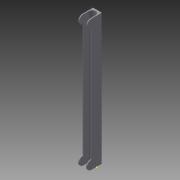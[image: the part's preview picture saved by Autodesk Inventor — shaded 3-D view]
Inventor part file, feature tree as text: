
AUTODESK INVENTOR PART (.ipt)
format: ipt  version: 2015 (Build 190159000, 159)  size: 121,856 bytes
history: native  units: mm
features: sketch x6, extrude x5, fillet x2
ambient origin geometry x8: Origin, YZ Plane, XZ Plane, XY Plane, X Axis, Y Axis, Z Axis, Center Point
bodies: Body1 (feature_tree)
feature tree (13):
  extrude  "Extrusion3"  Depth=1.0mm
  extrude  "Extrusion8"  Depth=150.0mm TaperAngle=0.0deg
  extrude  "Extrusion9"  Depth=10.0mm
  sketch  "Sketch11"  dims[d31=10.0mm d32=5.0mm]
  extrude  "Extrusion10"  Depth=5.0mm
  extrude  "Extrusion11"  Depth=10.0mm
  fillet  "Fillet4"  Radius=5.0mm
  fillet  "Fillet5"  Radius=1.0mm
  sketch  "Sketch3"  dims[d9=8.0mm d10=1.0mm]
  sketch  "Sketch9"  dims[d11=6.0mm d12=150.0mm d13=0.0mm]
  sketch  "Sketch10"  dims[d29=10.0mm d30=6.0mm]
  sketch  "Sketch12"  dims[d33=1.0mm d34=0.0mm d35=10.0mm d36=5.0mm d37=1.0mm d38=0.0mm]
  sketch  "Sketch13"  dims[d39=10.0mm d40=5.0mm d41=1.0mm d42=0.0mm d43=10.0mm d44=5.0mm d45=1.0mm d46=0.0mm d47=5.0mm d48=5.0mm]
